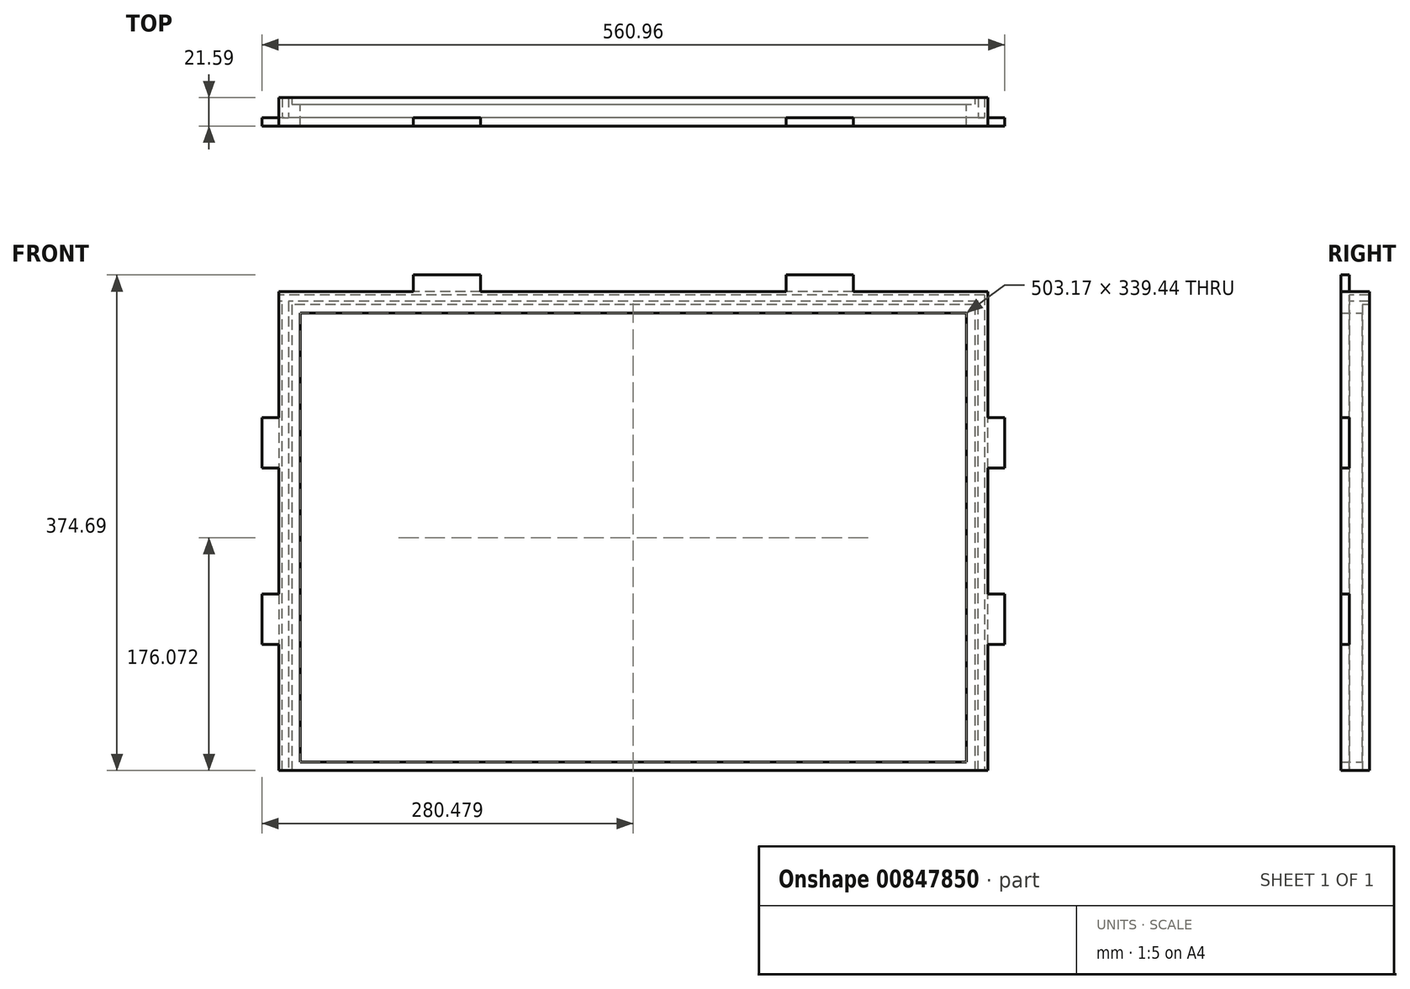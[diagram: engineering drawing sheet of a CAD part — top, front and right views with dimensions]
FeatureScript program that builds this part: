
annotation { "Feature Type Name" : "Feature", "Feature Type Description" : "" }
export const myFeature = defineFeature(function(context is Context, id is Id, definition is map)
    precondition{}
    {
        {
            var Q0;
            Q0=qCreatedBy(makeId("Front.planeOp"),FACE);
            var sketch = newSketch(context, id + "F0", { "sketchPlane" : qUnion([Q0])});
            skLineSegment(sketch, "E0.bottom", {"start": v(0, 0) * mm, "end": v(535.56, 0) * mm});
            skLineSegment(sketch, "E0.top", {"start": v(0, 361.99) * mm, "end": v(101.6, 361.99) * mm});
            skLineSegment(sketch, "E0.left", {"start": v(0, 0) * mm, "end": v(0, 95.25) * mm});
            skLineSegment(sketch, "E0.right", {"start": v(535.56, 0) * mm, "end": v(535.56, 95.25) * mm});
            skLineSegment(sketch, "E1.bottom", {"start": v(0, 95.25) * mm, "end": v(-12.7, 95.25) * mm});
            skLineSegment(sketch, "E1.top", {"start": v(0, 133.35) * mm, "end": v(-12.7, 133.35) * mm});
            skLineSegment(sketch, "E1.right", {"start": v(-12.7, 95.25) * mm, "end": v(-12.7, 133.35) * mm});
            skLineSegment(sketch, "E2.bottom", {"start": v(0, 228.64) * mm, "end": v(-12.7, 228.64) * mm});
            skLineSegment(sketch, "E2.top", {"start": v(0, 266.74) * mm, "end": v(-12.7, 266.74) * mm});
            skLineSegment(sketch, "E2.right", {"start": v(-12.7, 228.64) * mm, "end": v(-12.7, 266.74) * mm});
            skLineSegment(sketch, "E3.trimOffspring", {"start": v(0, 266.74) * mm, "end": v(0, 361.99) * mm});
            skLineSegment(sketch, "E4.trimOffspring", {"start": v(0, 133.35) * mm, "end": v(0, 228.64) * mm});
            skLineSegment(sketch, "E5.top", {"start": v(101.6, 374.69) * mm, "end": v(152.4, 374.69) * mm});
            skLineSegment(sketch, "E5.left", {"start": v(101.6, 361.99) * mm, "end": v(101.6, 374.69) * mm});
            skLineSegment(sketch, "E5.right", {"start": v(152.4, 361.99) * mm, "end": v(152.4, 374.69) * mm});
            skLineSegment(sketch, "E6.trimOffspring", {"start": v(152.4, 361.99) * mm, "end": v(383.16, 361.99) * mm});
            skLineSegment(sketch, "E7.MirrorCS", {"start": v(535.56, 228.64) * mm, "end": v(548.26, 228.64) * mm});
            skLineSegment(sketch, "E8.MirrorCS", {"start": v(535.56, 133.35) * mm, "end": v(548.26, 133.35) * mm});
            skLineSegment(sketch, "E9.MirrorCS", {"start": v(433.96, 361.99) * mm, "end": v(433.96, 374.69) * mm});
            skLineSegment(sketch, "E10.MirrorCS", {"start": v(383.16, 361.99) * mm, "end": v(383.16, 374.69) * mm});
            skLineSegment(sketch, "E11.MirrorCS", {"start": v(535.56, 95.25) * mm, "end": v(548.26, 95.25) * mm});
            skLineSegment(sketch, "E12.MirrorCS", {"start": v(535.56, 266.74) * mm, "end": v(548.26, 266.74) * mm});
            skLineSegment(sketch, "E13.MirrorCS", {"start": v(433.96, 374.69) * mm, "end": v(383.16, 374.69) * mm});
            skLineSegment(sketch, "E14.MirrorCS", {"start": v(535.56, 133.35) * mm, "end": v(535.56, 228.64) * mm});
            skLineSegment(sketch, "E15.MirrorCS", {"start": v(535.56, 361.99) * mm, "end": v(433.96, 361.99) * mm});
            skLineSegment(sketch, "E16.MirrorCS", {"start": v(535.56, 266.74) * mm, "end": v(535.56, 361.99) * mm});
            skLineSegment(sketch, "E17.MirrorCS", {"start": v(548.26, 228.64) * mm, "end": v(548.26, 266.74) * mm});
            skLineSegment(sketch, "E18.MirrorCS", {"start": v(548.26, 95.25) * mm, "end": v(548.26, 133.35) * mm});
            skLineSegment(sketch, "E19.trimOffspring", {"start": v(433.96, 361.99) * mm, "end": v(535.56, 361.99) * mm});
            skSolve(sketch);
        }
        {
            var Q0;
            Q0 = qSketchRegion(id + "F0", true);
            extrude(context, id + "F1", {"entities" : qUnion([Q0]), "depth" : 6.35 * mm, "offsetDistance" : 25.4 * mm});
        }
        {
            var Q0;
            Q0=makeQuery(id+"F1.opExtrude","CAP_FACE",FACE,{"disambiguationData":[OSD([sQuery(id+"F0.wireOp",EDGE,"E0.bottom"),sQuery(id+"F0.wireOp",EDGE,"E0.top"),sQuery(id+"F0.wireOp",EDGE,"E0.left"),sQuery(id+"F0.wireOp",EDGE,"E1.bottom"),sQuery(id+"F0.wireOp",EDGE,"E1.top"),sQuery(id+"F0.wireOp",EDGE,"E1.right"),sQuery(id+"F0.wireOp",EDGE,"E2.bottom"),sQuery(id+"F0.wireOp",EDGE,"E2.top"),sQuery(id+"F0.wireOp",EDGE,"E2.right"),sQuery(id+"F0.wireOp",EDGE,"E3.trimOffspring"),sQuery(id+"F0.wireOp",EDGE,"E4.trimOffspring"),sQuery(id+"F0.wireOp",EDGE,"E5.top"),sQuery(id+"F0.wireOp",EDGE,"E5.left"),sQuery(id+"F0.wireOp",EDGE,"E5.right"),sQuery(id+"F0.wireOp",EDGE,"E6.trimOffspring"),sQuery(id+"F0.wireOp",EDGE,"E7.MirrorCS"),sQuery(id+"F0.wireOp",EDGE,"E8.MirrorCS"),sQuery(id+"F0.wireOp",EDGE,"E9.MirrorCS"),sQuery(id+"F0.wireOp",EDGE,"E10.MirrorCS"),sQuery(id+"F0.wireOp",EDGE,"E11.MirrorCS"),sQuery(id+"F0.wireOp",EDGE,"E12.MirrorCS"),sQuery(id+"F0.wireOp",EDGE,"E0.right"),sQuery(id+"F0.wireOp",EDGE,"E13.MirrorCS"),sQuery(id+"F0.wireOp",EDGE,"E17.MirrorCS"),sQuery(id+"F0.wireOp",EDGE,"E18.MirrorCS"),sQuery(id+"F0.wireOp",EDGE,"E19.trimOffspring"),sQuery(id+"F0.wireOp",EDGE,"E16.MirrorCS"),sQuery(id+"F0.wireOp",EDGE,"E14.MirrorCS")])],"isStart":true});
            var sketch = newSketch(context, id + "F2", { "sketchPlane" : qUnion([Q0])});
            skLineSegment(sketch, "E20.bottom", {"start": v(-535.56, 361.99) * mm, "end": v(0, 361.99) * mm});
            skLineSegment(sketch, "E20.top", {"start": v(-533.02, 359.45) * mm, "end": v(-2.54, 359.45) * mm});
            skLineSegment(sketch, "E20.left", {"start": v(-535.56, 361.99) * mm, "end": v(-535.56, 359.45) * mm});
            skLineSegment(sketch, "E20.right", {"start": v(0, 361.99) * mm, "end": v(0, 359.45) * mm});
            skLineSegment(sketch, "E21.0.1.2", {"start": v(-535.56, 354.68) * mm, "end": v(-535.56, 352.14) * mm});
            skLineSegment(sketch, "E21.0.1.3", {"start": v(0, 354.68) * mm, "end": v(0, 352.14) * mm});
            skLineSegment(sketch, "E21.direction1", {"start": v(-533.02, 359.45) * mm, "end": v(-510.16, 359.45) * mm, "construction": true});
            skLineSegment(sketch, "E22.top", {"start": v(-535.56, 0) * mm, "end": v(-533.02, 0) * mm});
            skLineSegment(sketch, "E22.left", {"start": v(-535.56, 352.14) * mm, "end": v(-535.56, 0) * mm});
            skLineSegment(sketch, "E22.right", {"start": v(-533.02, 352.14) * mm, "end": v(-533.02, 0) * mm});
            skLineSegment(sketch, "E23.top", {"start": v(-528.26, 0) * mm, "end": v(-525.72, 0) * mm});
            skLineSegment(sketch, "E23.left", {"start": v(-528.26, 352.14) * mm, "end": v(-528.26, 0) * mm});
            skLineSegment(sketch, "E23.right", {"start": v(-525.72, 352.14) * mm, "end": v(-525.72, 0) * mm});
            skLineSegment(sketch, "E24", {"start": v(-528.26, 352.14) * mm, "end": v(-528.26, 354.68) * mm});
            skLineSegment(sketch, "E25", {"start": v(-533.02, 352.14) * mm, "end": v(-533.02, 354.68) * mm});
            skLineSegment(sketch, "E26.trimOffspring", {"start": v(-528.26, 354.68) * mm, "end": v(-7.3, 354.68) * mm});
            skLineSegment(sketch, "E27.trimOffspring", {"start": v(-525.72, 352.14) * mm, "end": v(-9.84, 352.14) * mm});
            skLineSegment(sketch, "E28", {"start": v(-533.02, 354.68) * mm, "end": v(-533.02, 359.45) * mm});
            skPoint(sketch, "E29", {"position": v(-267.78, 0) * mm});
            skLineSegment(sketch, "E30", {"start": v(-267.78, 0) * mm, "end": v(-267.78, 73.52) * mm});
            skLineSegment(sketch, "E31.MirrorCS", {"start": v(-2.54, 352.14) * mm, "end": v(-2.54, 354.68) * mm});
            skLineSegment(sketch, "E32.MirrorCS", {"start": v(0, 354.68) * mm, "end": v(0, 352.14) * mm, "construction": true});
            skLineSegment(sketch, "E33.MirrorCS", {"start": v(-7.3, 352.14) * mm, "end": v(-7.3, 354.68) * mm});
            skLineSegment(sketch, "E34.MirrorCS", {"start": v(0, 0) * mm, "end": v(-2.54, 0) * mm});
            skLineSegment(sketch, "E35.MirrorCS", {"start": v(-7.3, 0) * mm, "end": v(-9.84, 0) * mm});
            skLineSegment(sketch, "E36.MirrorCS", {"start": v(-9.84, 352.14) * mm, "end": v(-9.84, 0) * mm});
            skLineSegment(sketch, "E37.MirrorCS", {"start": v(-7.3, 352.14) * mm, "end": v(-7.3, 0) * mm});
            skLineSegment(sketch, "E38.MirrorCS", {"start": v(0, 352.14) * mm, "end": v(0, 0) * mm});
            skLineSegment(sketch, "E39.MirrorCS", {"start": v(-2.54, 352.14) * mm, "end": v(-2.54, 0) * mm});
            skLineSegment(sketch, "E40", {"start": v(-2.54, 354.68) * mm, "end": v(0, 354.68) * mm});
            skLineSegment(sketch, "E41", {"start": v(-2.54, 359.45) * mm, "end": v(0, 359.45) * mm});
            skLineSegment(sketch, "E42", {"start": v(-535.56, 359.45) * mm, "end": v(-535.56, 354.68) * mm});
            skSolve(sketch);
        }
        {
            var Q0;
            Q0 = qSketchRegion(id + "F2", true);
            extrude(context, id + "F3", {"entities" : qUnion([Q0]), "operationType" : NewBodyOperationType.ADD, "depth" : 15.24 * mm, "offsetDistance" : 25.4 * mm});
        }
        {
            var Q0;
            {var subQ0=sQuery(id+"F0.wireOp",EDGE,"E0.bottom");Q0=makeQuery(id+"F3.boolean.opBoolean","SPLIT",FACE,{"disambiguationData":[TD([makeQuery(id+"F3.opExtrude","SWEPT_FACE",FACE,{"disambiguationData":[OSD([sQuery(id+"F2.wireOp",EDGE,"E23.right")])]})])],"derivedFrom":makeQuery(id+"F1.opExtrude","CAP_FACE",FACE,{"disambiguationData":[OSD([subQ0,sQuery(id+"F0.wireOp",EDGE,"E0.top"),sQuery(id+"F0.wireOp",EDGE,"E0.left"),sQuery(id+"F0.wireOp",EDGE,"E1.bottom"),sQuery(id+"F0.wireOp",EDGE,"E1.top"),sQuery(id+"F0.wireOp",EDGE,"E1.right"),sQuery(id+"F0.wireOp",EDGE,"E2.bottom"),sQuery(id+"F0.wireOp",EDGE,"E2.top"),sQuery(id+"F0.wireOp",EDGE,"E2.right"),sQuery(id+"F0.wireOp",EDGE,"E3.trimOffspring"),sQuery(id+"F0.wireOp",EDGE,"E4.trimOffspring"),sQuery(id+"F0.wireOp",EDGE,"E5.top"),sQuery(id+"F0.wireOp",EDGE,"E5.left"),sQuery(id+"F0.wireOp",EDGE,"E5.right"),sQuery(id+"F0.wireOp",EDGE,"E6.trimOffspring"),sQuery(id+"F0.wireOp",EDGE,"E7.MirrorCS"),sQuery(id+"F0.wireOp",EDGE,"E8.MirrorCS"),sQuery(id+"F0.wireOp",EDGE,"E9.MirrorCS"),sQuery(id+"F0.wireOp",EDGE,"E10.MirrorCS"),sQuery(id+"F0.wireOp",EDGE,"E11.MirrorCS"),sQuery(id+"F0.wireOp",EDGE,"E12.MirrorCS"),sQuery(id+"F0.wireOp",EDGE,"E0.right"),sQuery(id+"F0.wireOp",EDGE,"E13.MirrorCS"),sQuery(id+"F0.wireOp",EDGE,"E17.MirrorCS"),sQuery(id+"F0.wireOp",EDGE,"E18.MirrorCS"),sQuery(id+"F0.wireOp",EDGE,"E19.trimOffspring"),sQuery(id+"F0.wireOp",EDGE,"E16.MirrorCS"),sQuery(id+"F0.wireOp",EDGE,"E14.MirrorCS")])],"isStart":true})});}
            var sketch = newSketch(context, id + "F4", { "sketchPlane" : qUnion([Q0])});
            skLineSegment(sketch, "E43.bottom", {"start": v(-525.72, 352.14) * mm, "end": v(-9.84, 352.14) * mm});
            skLineSegment(sketch, "E43.top", {"start": v(-525.72, 0) * mm, "end": v(-9.84, 0) * mm});
            skLineSegment(sketch, "E43.left", {"start": v(-525.72, 352.14) * mm, "end": v(-525.72, 0) * mm});
            skLineSegment(sketch, "E43.right", {"start": v(-9.84, 352.14) * mm, "end": v(-9.84, 0) * mm});
            skSolve(sketch);
        }
        {
            var Q0;
            Q0 = qSketchRegion(id + "F4", true);
            extrude(context, id + "F5", {"entities" : qUnion([Q0]), "operationType" : NewBodyOperationType.ADD, "depth" : 9.98 * mm, "offsetDistance" : 25.4 * mm});
        }
        {
            var Q0;
            Q0=makeQuery(id+"F5.opExtrude","CAP_FACE",FACE,{"disambiguationData":[OSD([sQuery(id+"F4.wireOp",EDGE,"E43.bottom"),sQuery(id+"F4.wireOp",EDGE,"E43.top"),sQuery(id+"F4.wireOp",EDGE,"E43.left"),sQuery(id+"F4.wireOp",EDGE,"E43.right")])],"isStart":false});
            var sketch = newSketch(context, id + "F6", { "sketchPlane" : qUnion([Q0])});
            skLineSegment(sketch, "E44.0", {"start": v(-525.72, 352.14) * mm, "end": v(-525.72, 0) * mm});
            skLineSegment(sketch, "E45.0", {"start": v(-519.37, 345.8) * mm, "end": v(-519.37, 6.35) * mm});
            skLineSegment(sketch, "E46.0", {"start": v(-16.2, 345.8) * mm, "end": v(-519.37, 345.8) * mm});
            skLineSegment(sketch, "E46.1", {"start": v(-16.2, 6.35) * mm, "end": v(-16.2, 345.8) * mm});
            skLineSegment(sketch, "E47", {"start": v(-519.37, 6.35) * mm, "end": v(-16.2, 6.35) * mm});
            skSolve(sketch);
        }
        {
            var Q0;
            Q0 = qSketchRegion(id + "F6", true);
            extrude(context, id + "F7", {"entities" : qUnion([Q0]), "operationType" : NewBodyOperationType.REMOVE, "endBound" : BoundingType.THROUGH_ALL, "oppositeDirection" : true, "depth" : 25.4 * mm, "offsetDistance" : 25.4 * mm});
        }
    });
